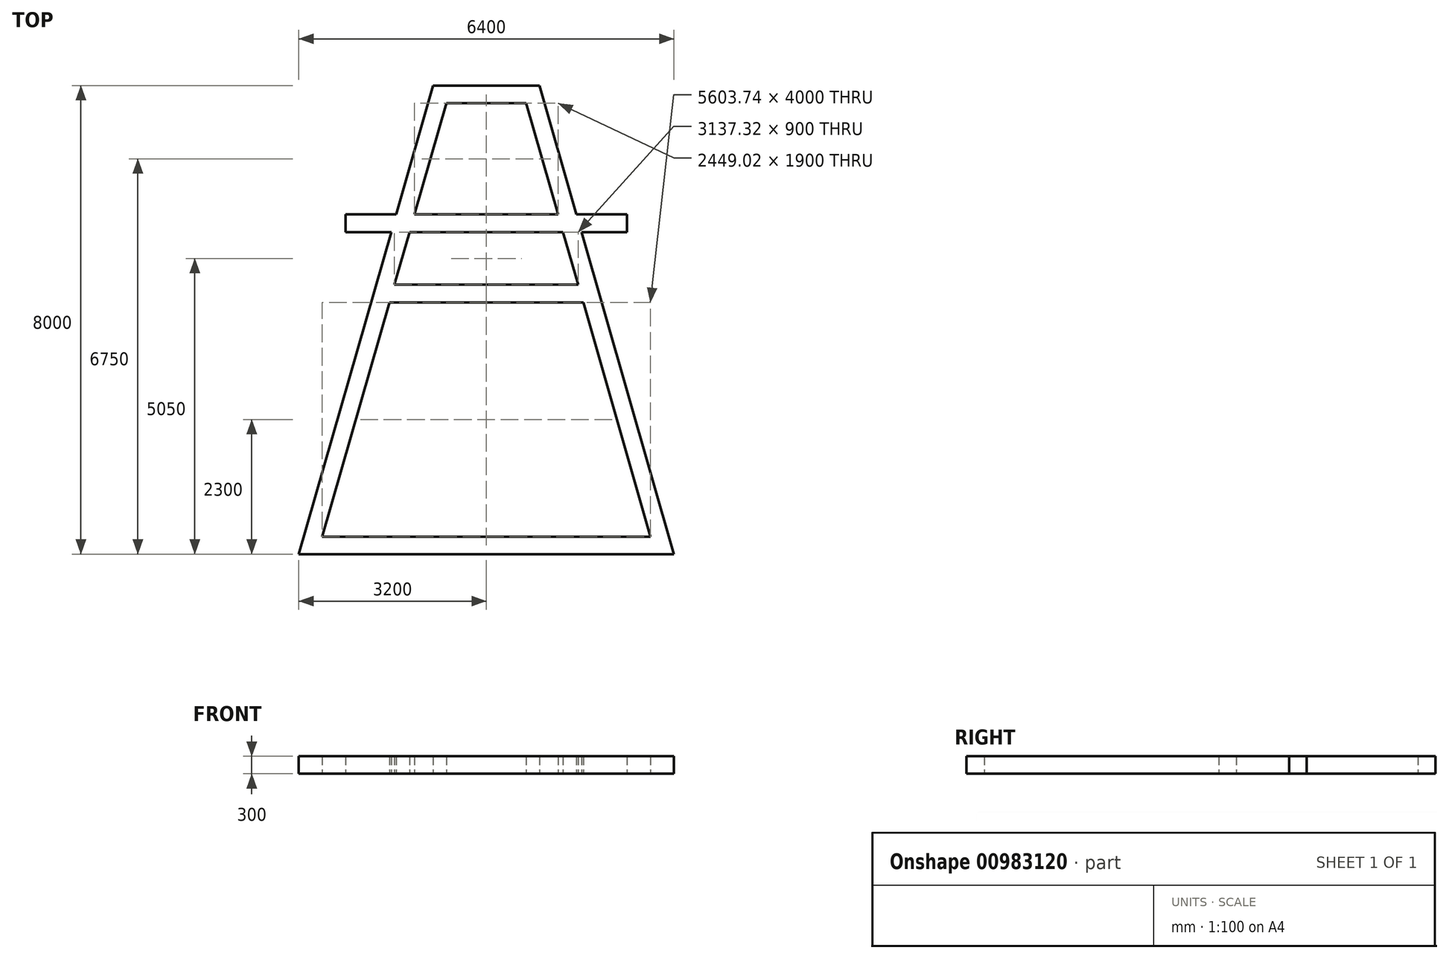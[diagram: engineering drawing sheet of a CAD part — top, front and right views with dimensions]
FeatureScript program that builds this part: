
annotation { "Feature Type Name" : "Feature", "Feature Type Description" : "" }
export const myFeature = defineFeature(function(context is Context, id is Id, definition is map)
    precondition{}
    {
        {
            var Q0;
            Q0=qCreatedBy(makeId("Top.planeOp"),FACE);
            var sketch = newSketch(context, id + "F0", { "sketchPlane" : qUnion([Q0])});
            skLineSegment(sketch, "E0", {"start": v(0, -5060.64) * mm, "end": v(0, 5279.25) * mm, "construction": true});
            skLineSegment(sketch, "E1", {"start": v(-1622.64, 2200) * mm, "end": v(-3200, -3300) * mm});
            skLineSegment(sketch, "E2", {"start": v(-3200, -3300) * mm, "end": v(0, -3300) * mm});
            skLineSegment(sketch, "E3", {"start": v(0, 2200) * mm, "end": v(-1310.55, 2200) * mm});
            skLineSegment(sketch, "E4", {"start": v(-1310.55, 2200) * mm, "end": v(-1568.66, 1300) * mm});
            skLineSegment(sketch, "E5", {"start": v(-2801.87, -3000) * mm, "end": v(0, -3000) * mm});
            skLineSegment(sketch, "E6", {"start": v(0, -3000) * mm, "end": v(0, -3300) * mm});
            skLineSegment(sketch, "E7", {"start": v(-1536.6, 2500) * mm, "end": v(-905.66, 4700) * mm});
            skLineSegment(sketch, "E8", {"start": v(-905.66, 4700) * mm, "end": v(0, 4700) * mm});
            skLineSegment(sketch, "E9", {"start": v(0, 4700) * mm, "end": v(0, 4400) * mm});
            skLineSegment(sketch, "E10", {"start": v(0, 4400) * mm, "end": v(-679.6, 4400) * mm});
            skLineSegment(sketch, "E11", {"start": v(-1224.51, 2500) * mm, "end": v(-679.6, 4400) * mm});
            skLineSegment(sketch, "E12", {"start": v(0, 2500) * mm, "end": v(-1224.51, 2500) * mm});
            skLineSegment(sketch, "E13", {"start": v(-2400, 2500) * mm, "end": v(-2400, 2200) * mm});
            skLineSegment(sketch, "E14", {"start": v(-2400, 2200) * mm, "end": v(-1622.64, 2200) * mm});
            skLineSegment(sketch, "E15", {"start": v(-1568.66, 1300) * mm, "end": v(0, 1300) * mm});
            skLineSegment(sketch, "E16", {"start": v(0, 1300) * mm, "end": v(0, 1000) * mm});
            skLineSegment(sketch, "E17", {"start": v(0, 1000) * mm, "end": v(-1654.7, 1000) * mm});
            skLineSegment(sketch, "E18.trimOffspring", {"start": v(-1654.7, 1000) * mm, "end": v(-2801.87, -3000) * mm});
            skLineSegment(sketch, "E19.trimOffspring", {"start": v(-1536.6, 2500) * mm, "end": v(-2400, 2500) * mm});
            skLineSegment(sketch, "E20", {"start": v(0, 2500) * mm, "end": v(0, 2200) * mm});
            skSolve(sketch);
        }
        {
            var Q0;
            Q0 = qSketchRegion(id + "F0", true);
            extrude(context, id + "F1", {"entities" : qUnion([Q0]), "depth" : 300 * mm, "offsetDistance" : 25 * mm});
        }
        {
            var Q0;
            Q0=makeQuery(id+"F1.opExtrude","SWEPT_BODY",BODY,{"disambiguationData":[OSD([sQuery(id+"F0.wireOp",EDGE,"E1"),sQuery(id+"F0.wireOp",EDGE,"E2"),sQuery(id+"F0.wireOp",EDGE,"E3"),sQuery(id+"F0.wireOp",EDGE,"E4"),sQuery(id+"F0.wireOp",EDGE,"E5"),sQuery(id+"F0.wireOp",EDGE,"E6"),sQuery(id+"F0.wireOp",EDGE,"E7"),sQuery(id+"F0.wireOp",EDGE,"E8"),sQuery(id+"F0.wireOp",EDGE,"E9"),sQuery(id+"F0.wireOp",EDGE,"E10"),sQuery(id+"F0.wireOp",EDGE,"E11"),sQuery(id+"F0.wireOp",EDGE,"E12"),sQuery(id+"F0.wireOp",EDGE,"E13"),sQuery(id+"F0.wireOp",EDGE,"E14"),sQuery(id+"F0.wireOp",EDGE,"E15"),sQuery(id+"F0.wireOp",EDGE,"E16"),sQuery(id+"F0.wireOp",EDGE,"E17"),sQuery(id+"F0.wireOp",EDGE,"E18.trimOffspring"),sQuery(id+"F0.wireOp",EDGE,"E19.trimOffspring"),sQuery(id+"F0.wireOp",EDGE,"E20")])]});
            var Q1;
            Q1=qCreatedBy(makeId("Right.planeOp"),FACE);
            mirror(context, id + "F2", {"operationType" : NewBodyOperationType.ADD, "entities" : qUnion([Q0]), "mirrorPlane" : qUnion([Q1])});
        }
    });
